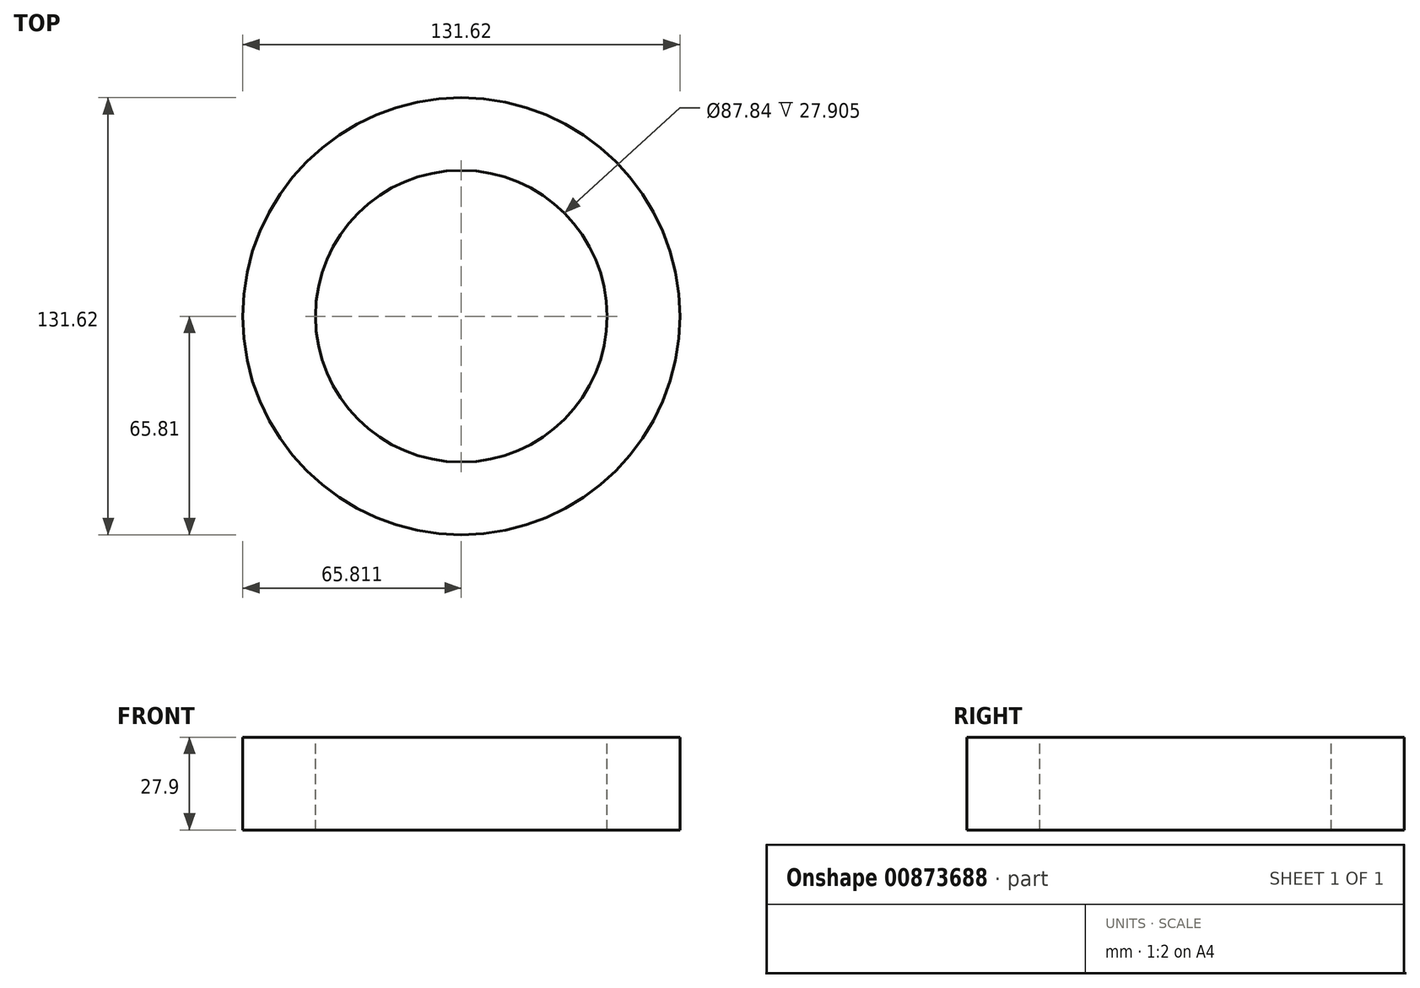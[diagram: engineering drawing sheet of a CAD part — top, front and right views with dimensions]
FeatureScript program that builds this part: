
annotation { "Feature Type Name" : "Feature", "Feature Type Description" : "" }
export const myFeature = defineFeature(function(context is Context, id is Id, definition is map)
    precondition{}
    {
        {
            var Q0;
            Q0=qCreatedBy(makeId("Front.planeOp"),FACE);
            var sketch = newSketch(context, id + "F0", { "sketchPlane" : qUnion([Q0])});
            skLineSegment(sketch, "E0.left", {"start": v(-0.02, 0.5) * mm, "end": v(-0.02, -0.86) * mm});
            skPoint(sketch, "E0.middle", {"position": v(0, 0) * mm});
            skLineSegment(sketch, "E1.bottom", {"start": v(65.8, 13.95) * mm, "end": v(43.9, 13.95) * mm});
            skLineSegment(sketch, "E1.top", {"start": v(65.8, -13.95) * mm, "end": v(43.9, -13.95) * mm});
            skLineSegment(sketch, "E1.left", {"start": v(65.8, 13.95) * mm, "end": v(65.8, -13.95) * mm});
            skLineSegment(sketch, "E1.right", {"start": v(43.9, 13.95) * mm, "end": v(43.9, -13.95) * mm});
            skPoint(sketch, "E1.middle", {"position": v(54.85, 0) * mm});
            skSolve(sketch);
        }
        {
            var Q0;
            Q0=makeQuery(id+"F0.imprint","IMPRINT",FACE,{"disambiguationData":[TD([[makeQuery(id+"F0.imprint","IMPRINT",EDGE,{"derivedFrom":sQuery(id+"F0.wireOp",EDGE,"E1.bottom")}),1.0]])]});
            var Q1;
            Q1=sQuery(id+"F0.wireOp",EDGE,"E0.left");
            revolve(context, id + "F1", {"surfaceOperationType" : NewSurfaceOperationType.NEW, "entities" : qUnion([Q0]), "axis" : qUnion([Q1]), "revolveType" : RevolveType.FULL});
        }
    });
